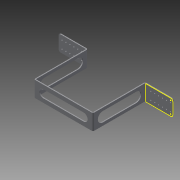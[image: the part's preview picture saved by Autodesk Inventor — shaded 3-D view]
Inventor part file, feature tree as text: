
AUTODESK INVENTOR PART (.ipt)
format: ipt  version: 2014 SP1 (Build 180222100, 222)  size: 379,904 bytes
history: native  units: in
note: dims shown in document units (in); Inventor stores cm internally (conversion verified against a paired STEP export)
features: sheet_metal_op x7, sketch x7, other x6, reference x3, extrude x2, chamfer x1
ambient origin geometry x8: Origin, YZ Plane, XZ Plane, XY Plane, X Axis, Y Axis, Z Axis, Center Point
bodies: Solid1 (feature_tree)
feature tree (26):
  sheet_metal_op  "Face1"
  sheet_metal_op  "Flange1"
  sheet_metal_op  "Flange2"
  chamfer  "Corner Round1"
  sketch  "Sketch4"  dims[d5=0.25in]
  extrude  "Extrusion1"  Depth=2.0in
  sketch  "Sketch1"  dims[d0=7.25in d1=2.0in]
  other  "Plate1"
  sketch  "Sketch2"  dims[d2=0.125in d3=0.125in]
  other  "Plate2"
  sheet_metal_op  "Bend1"
  sheet_metal_op  "Corner1"
  sketch  "Sketch3"  dims[d4=0.0625in]
  other  "Plate3"
  sheet_metal_op  "Bend2"
  sheet_metal_op  "Corner2"
  sketch  "Sketch5"  dims[d6=0.125in]
  reference  "Reference1"
  reference  "Reference2"
  reference  "Reference3"
  sketch  "Sketch6"  dims[d7=6.5in d8=90.0deg d9=0.05in]
  sketch  "Sketch7"  dims[d10=0.5in d11=0.125in d12=0.125in d13=0.125in d14=0.0625in d15=0.25in d16=0.125in d17=3.5in d18=90.0deg d19=0.05in d20=0.5in d21=0.125in d22=0.125in d23=0.25in d24=0.125in d25=0.0in d26=1.25in d27=1.0in d28=1.0665in d29=100.0in d30=0.0in d31=5.15in d32=1.0in d33=1.0in d34=1.0in d35=0.125in d36=0.0in]
  other  "Cut1"
  other  "Cut2"
  other  "Definition1"
  extrude  "Extrusion2"  Depth=0.125in
